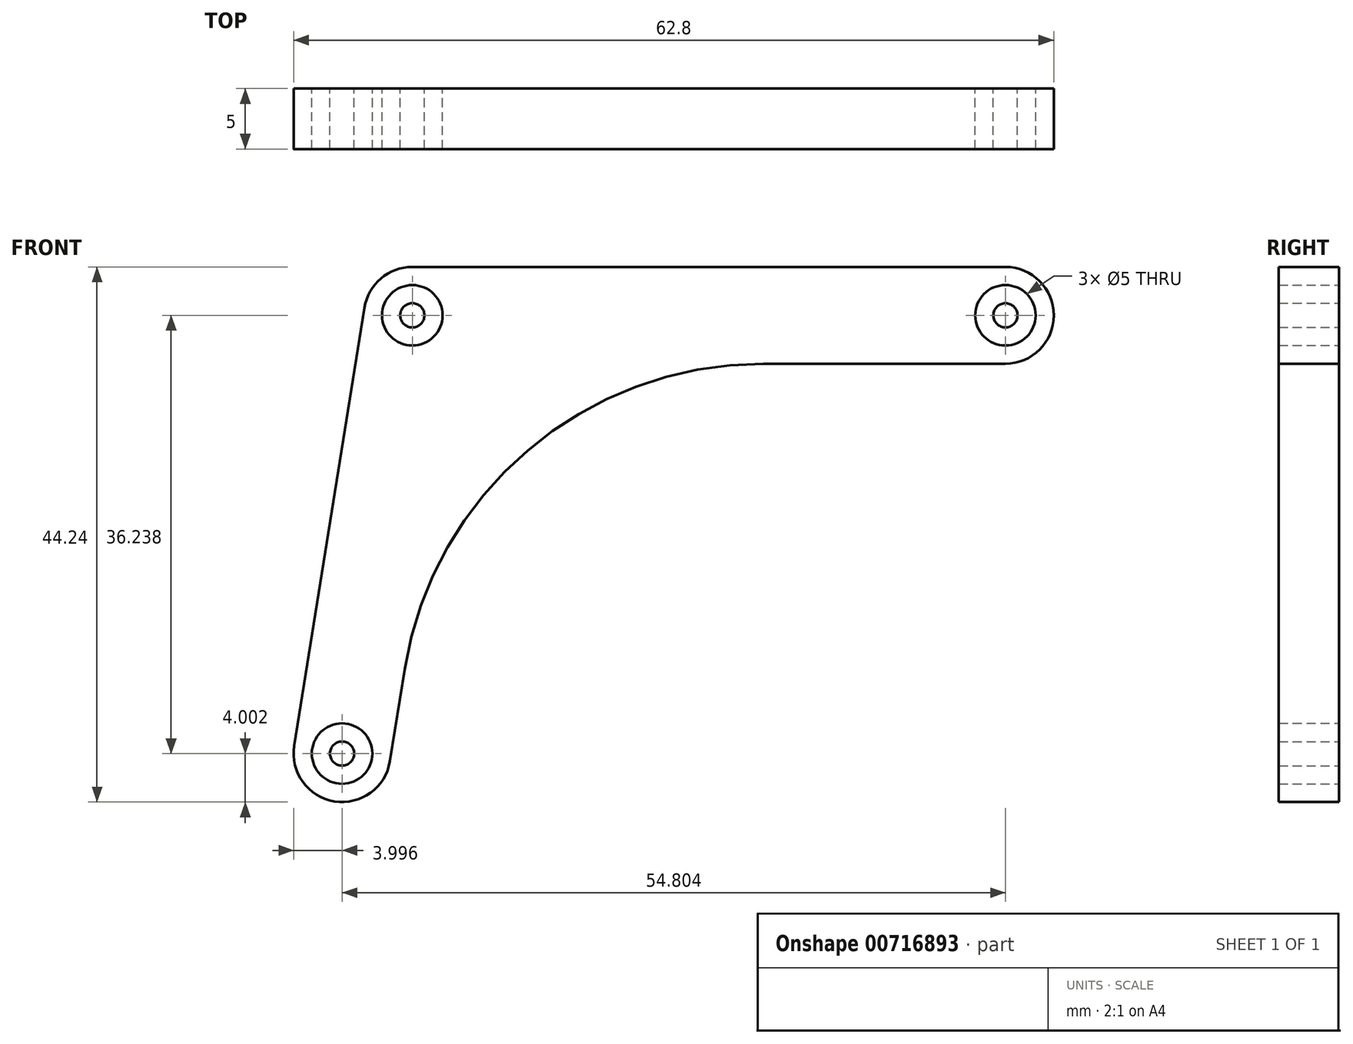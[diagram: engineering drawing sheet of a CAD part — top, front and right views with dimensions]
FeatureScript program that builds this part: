
annotation { "Feature Type Name" : "Feature", "Feature Type Description" : "" }
export const myFeature = defineFeature(function(context is Context, id is Id, definition is map)
    precondition{}
    {
        {
            var Q0;
            Q0=qCreatedBy(makeId("Front.planeOp"),FACE);
            var sketch = newSketch(context, id + "F0", { "sketchPlane" : qUnion([Q0])});
            skArc(sketch, "E0", {"start": v(0, -4) * mm, "mid": v(4, 0) * mm, "end": v(0, 4) * mm});
            skArc(sketch, "E1", {"start": v(-49, 4) * mm, "mid": v(-51.6, 3.04) * mm, "end": v(-52.95, 0.63) * mm});
            skArc(sketch, "E2", {"start": v(-58.75, -35.6) * mm, "mid": v(-55.44, -40.19) * mm, "end": v(-50.85, -36.87) * mm});
            skLineSegment(sketch, "E3", {"start": v(0, 4) * mm, "end": v(-49, 4) * mm});
            skLineSegment(sketch, "E4", {"start": v(0, -4) * mm, "end": v(-20.01, -4) * mm});
            skLineSegment(sketch, "E5", {"start": v(-52.95, 0.63) * mm, "end": v(-58.75, -35.6) * mm});
            skLineSegment(sketch, "E6", {"start": v(-49.63, -29.26) * mm, "end": v(-50.85, -36.87) * mm});
            skArc(sketch, "E7.filletArc", {"start": v(-20.01, -4) * mm, "mid": v(-39.48, -11.17) * mm, "end": v(-49.63, -29.26) * mm});
            skCircle(sketch, "E8", {"center": v(-49, 0) * mm, "radius": 2.5 * mm});
            skCircle(sketch, "E9", {"center": v(0, 0) * mm, "radius": 2.5 * mm});
            skCircle(sketch, "E10", {"center": v(-54.8, -36.24) * mm, "radius": 2.5 * mm});
            skCircle(sketch, "E11", {"center": v(0, 0) * mm, "radius": 1 * mm});
            skCircle(sketch, "E12", {"center": v(-49, 0) * mm, "radius": 1 * mm});
            skCircle(sketch, "E13", {"center": v(-54.8, -36.24) * mm, "radius": 1 * mm});
            skSolve(sketch);
        }
        {
            var Q0;
            Q0 = qSketchRegion(id + "F0", true);
            var Q1;
            Q1=makeQuery(id+"F0.imprint","IMPRINT",FACE,{"disambiguationData":[TD([[makeQuery(id+"F0.imprint","IMPRINT",EDGE,{"derivedFrom":sQuery(id+"F0.wireOp",EDGE,"E12")}),1.0]])]});
            var Q2;
            Q2=makeQuery(id+"F0.imprint","IMPRINT",FACE,{"disambiguationData":[TD([[makeQuery(id+"F0.imprint","IMPRINT",EDGE,{"derivedFrom":sQuery(id+"F0.wireOp",EDGE,"E11")}),1.0]])]});
            var Q3;
            Q3=makeQuery(id+"F0.imprint","IMPRINT",FACE,{"disambiguationData":[TD([[makeQuery(id+"F0.imprint","IMPRINT",EDGE,{"derivedFrom":sQuery(id+"F0.wireOp",EDGE,"E13")}),1.0]])]});
            extrude(context, id + "F1", {"entities" : qUnion([Q0, Q1, Q2, Q3]), "depth" : 5 * mm, "offsetDistance" : 25.4 * mm});
        }
    });
